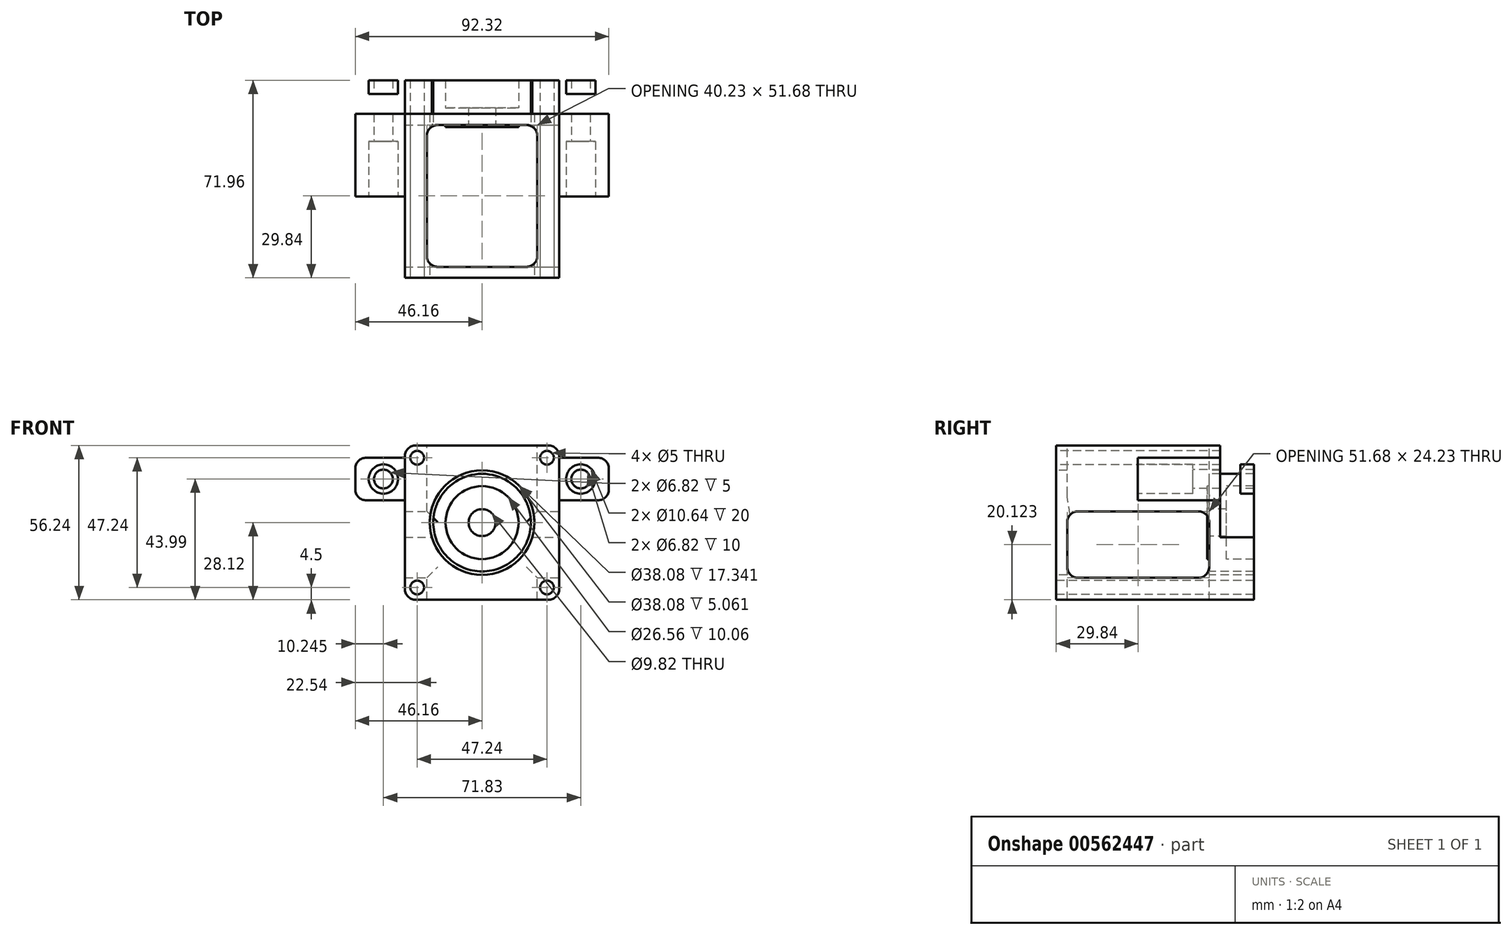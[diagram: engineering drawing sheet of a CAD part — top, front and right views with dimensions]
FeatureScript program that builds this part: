
annotation { "Feature Type Name" : "Feature", "Feature Type Description" : "" }
export const myFeature = defineFeature(function(context is Context, id is Id, definition is map)
    precondition{}
    {
        {
            var Q0;
            Q0=qCreatedBy(makeId("Front.planeOp"),FACE);
            var sketch = newSketch(context, id + "F0", { "sketchPlane" : qUnion([Q0])});
            skLineSegment(sketch, "E0.rect.bottom", {"start": v(-28.11, 28.11) * mm, "end": v(28.12, 28.11) * mm});
            skLineSegment(sketch, "E0.rect.top", {"start": v(-28.12, -28.11) * mm, "end": v(28.11, -28.11) * mm});
            skLineSegment(sketch, "E0.rect.left", {"start": v(-28.11, 28.12) * mm, "end": v(-28.12, -28.11) * mm});
            skLineSegment(sketch, "E0.rect.right", {"start": v(28.12, 28.11) * mm, "end": v(28.11, -28.11) * mm});
            skPoint(sketch, "E0.rect.middle", {"position": v(0, 0) * mm});
            skCircle(sketch, "E1", {"center": v(0, 0) * mm, "radius": 19.04 * mm});
            skCircle(sketch, "E2", {"center": v(0, 0) * mm, "radius": 3.98 * mm});
            skCircle(sketch, "E3", {"center": v(-23.62, 23.62) * mm, "radius": 2.5 * mm});
            skCircle(sketch, "E4", {"center": v(23.62, 23.62) * mm, "radius": 2.5 * mm});
            skCircle(sketch, "E5", {"center": v(23.62, -23.62) * mm, "radius": 2.5 * mm});
            skCircle(sketch, "E6", {"center": v(-23.62, -23.62) * mm, "radius": 2.5 * mm});
            skLineSegment(sketch, "E7.rect.bottom", {"start": v(-23.62, 23.62) * mm, "end": v(23.62, 23.62) * mm, "construction": true});
            skLineSegment(sketch, "E7.rect.top", {"start": v(-23.62, -23.62) * mm, "end": v(23.62, -23.62) * mm, "construction": true});
            skLineSegment(sketch, "E7.rect.left", {"start": v(-23.62, 23.62) * mm, "end": v(-23.62, -23.62) * mm, "construction": true});
            skLineSegment(sketch, "E7.rect.right", {"start": v(23.62, 23.62) * mm, "end": v(23.62, -23.62) * mm, "construction": true});
            skCircle(sketch, "E8", {"center": v(0, 0) * mm, "radius": 5.38 * mm});
            skSolve(sketch);
        }
        {
            var Q0;
            Q0=qCreatedBy(makeId("Front.planeOp"),FACE);
            var sketch = newSketch(context, id + "F1", { "sketchPlane" : qUnion([Q0])});
            skLineSegment(sketch, "E9.bottom", {"start": v(46.15, 37.06) * mm, "end": v(-46.16, 37.06) * mm});
            skLineSegment(sketch, "E9.top", {"start": v(46.16, -5.28) * mm, "end": v(-46.16, -5.28) * mm});
            skLineSegment(sketch, "E9.left", {"start": v(46.15, 37.06) * mm, "end": v(46.16, -5.28) * mm});
            skLineSegment(sketch, "E9.right", {"start": v(-46.16, 37.06) * mm, "end": v(-46.16, -5.28) * mm});
            skCircle(sketch, "E10", {"center": v(0, 0) * mm, "radius": 13.28 * mm});
            skCircle(sketch, "E11", {"center": v(-35.92, 15.87) * mm, "radius": 3.41 * mm});
            skCircle(sketch, "E12", {"center": v(35.91, 15.87) * mm, "radius": 3.41 * mm});
            skCircle(sketch, "E13", {"center": v(-35.92, 15.87) * mm, "radius": 5.32 * mm});
            skCircle(sketch, "E14", {"center": v(35.91, 15.87) * mm, "radius": 5.32 * mm});
            skSolve(sketch);
        }
        {
            var Q0;
            Q0=qCreatedBy(makeId("Front.planeOp"),FACE);
            var sketch = newSketch(context, id + "F2", { "sketchPlane" : qUnion([Q0])});
            skCircle(sketch, "E15", {"center": v(0, 0) * mm, "radius": 4.91 * mm});
            skCircle(sketch, "E16", {"center": v(0, 0) * mm, "radius": 13.28 * mm});
            skCircle(sketch, "E17", {"center": v(0, 0) * mm, "radius": 17.77 * mm});
            skSolve(sketch);
        }
        {
            var Q0;
            Q0=qCreatedBy(makeId("Front.planeOp"),FACE);
            var sketch = newSketch(context, id + "F3", { "sketchPlane" : qUnion([Q0])});
            skLineSegment(sketch, "E18.bottom", {"start": v(-28.11, 28.11) * mm, "end": v(28.12, 28.11) * mm});
            skLineSegment(sketch, "E18.top", {"start": v(-28.11, -5.28) * mm, "end": v(28.12, -5.28) * mm});
            skLineSegment(sketch, "E18.left", {"start": v(-28.11, 28.11) * mm, "end": v(-28.11, -5.28) * mm});
            skLineSegment(sketch, "E18.right", {"start": v(28.12, 28.12) * mm, "end": v(28.12, -5.28) * mm});
            skLineSegment(sketch, "E19.bottom", {"start": v(-28.11, -5.28) * mm, "end": v(28.11, -5.28) * mm});
            skLineSegment(sketch, "E19.top", {"start": v(-28.12, -28.11) * mm, "end": v(28.11, -28.11) * mm});
            skLineSegment(sketch, "E19.left", {"start": v(-28.11, -5.28) * mm, "end": v(-28.11, -28.11) * mm});
            skLineSegment(sketch, "E19.right", {"start": v(28.11, -5.28) * mm, "end": v(28.11, -28.11) * mm});
            skCircle(sketch, "E20", {"center": v(0, 0) * mm, "radius": 19.04 * mm});
            skCircle(sketch, "E21", {"center": v(-23.62, 23.62) * mm, "radius": 2.5 * mm});
            skCircle(sketch, "E22", {"center": v(23.62, 23.62) * mm, "radius": 2.5 * mm});
            skCircle(sketch, "E23", {"center": v(-23.62, -23.62) * mm, "radius": 2.5 * mm});
            skCircle(sketch, "E24", {"center": v(23.62, -23.62) * mm, "radius": 2.5 * mm});
            skLineSegment(sketch, "E25.bottom", {"start": v(46.15, 23.62) * mm, "end": v(28.11, 23.62) * mm});
            skLineSegment(sketch, "E25.top", {"start": v(46.15, 8.12) * mm, "end": v(28.12, 8.12) * mm});
            skLineSegment(sketch, "E25.left", {"start": v(46.15, 23.62) * mm, "end": v(46.15, 8.12) * mm});
            skLineSegment(sketch, "E25.right", {"start": v(28.12, 23.62) * mm, "end": v(28.12, 8.12) * mm});
            skLineSegment(sketch, "E26.bottom", {"start": v(-28.11, 23.62) * mm, "end": v(-46.16, 23.62) * mm});
            skLineSegment(sketch, "E26.top", {"start": v(-28.11, 8.12) * mm, "end": v(-46.16, 8.12) * mm});
            skLineSegment(sketch, "E26.left", {"start": v(-28.11, 23.62) * mm, "end": v(-28.11, 8.12) * mm});
            skLineSegment(sketch, "E26.right", {"start": v(-46.16, 23.62) * mm, "end": v(-46.16, 8.12) * mm});
            skCircle(sketch, "E27", {"center": v(35.91, 15.87) * mm, "radius": 3.41 * mm});
            skCircle(sketch, "E28", {"center": v(35.91, 15.87) * mm, "radius": 5.32 * mm});
            skCircle(sketch, "E29", {"center": v(-35.92, 15.87) * mm, "radius": 5.32 * mm});
            skCircle(sketch, "E30", {"center": v(-35.92, 15.87) * mm, "radius": 3.41 * mm});
            skSolve(sketch);
        }
        {
            var Q0;
            Q0=makeQuery(id+"F3.imprint","IMPRINT",FACE,{"disambiguationData":[TD([[makeQuery(id+"F3.imprint","IMPRINT",EDGE,{"derivedFrom":sQuery(id+"F3.wireOp",EDGE,"E19.top")}),1.0]])]});
            var Q1;
            Q1=makeQuery(id+"FeMlEP8lejCZseU_0.opExtrude","CAP_FACE",FACE,{"disambiguationData":[OSD([sQuery(id+"F1.wireOp",EDGE,"E9.bottom"),sQuery(id+"F1.wireOp",EDGE,"E9.top"),sQuery(id+"F1.wireOp",EDGE,"E9.left"),sQuery(id+"F1.wireOp",EDGE,"E9.right"),sQuery(id+"F1.wireOp",EDGE,"E10"),sQuery(id+"F1.wireOp",EDGE,"E13"),sQuery(id+"F1.wireOp",EDGE,"E14")])],"isStart":false});
            extrude(context, id + "F4", {"entities" : qUnion([Q0]), "oppositeDirection" : true, "endBoundEntityFace" : qUnion([Q1]), "depth" : 42.28 * mm, "hasSecondDirection" : true, "secondDirectionOppositeDirection" : false, "secondDirectionDepth" : 29.68 * mm});
        }
        {
            var Q0;
            Q0=makeQuery(id+"F3.imprint","IMPRINT",FACE,{"disambiguationData":[TD([[makeQuery(id+"F3.imprint","IMPRINT",EDGE,{"derivedFrom":sQuery(id+"F3.wireOp",EDGE,"E18.bottom")}),-1.0]])]});
            var Q1;
            Q1=makeQuery(id+"FeMlEP8lejCZseU_0.opExtrude","CAP_FACE",FACE,{"disambiguationData":[OSD([sQuery(id+"F1.wireOp",EDGE,"E9.bottom"),sQuery(id+"F1.wireOp",EDGE,"E9.top"),sQuery(id+"F1.wireOp",EDGE,"E9.left"),sQuery(id+"F1.wireOp",EDGE,"E9.right"),sQuery(id+"F1.wireOp",EDGE,"E10"),sQuery(id+"F1.wireOp",EDGE,"E13"),sQuery(id+"F1.wireOp",EDGE,"E14")])],"isStart":true});
            extrude(context, id + "F5", {"entities" : qUnion([Q0]), "operationType" : NewBodyOperationType.ADD, "oppositeDirection" : true, "endBoundEntityFace" : qUnion([Q1]), "depth" : 30 * mm, "hasSecondDirection" : true, "secondDirectionOppositeDirection" : false, "secondDirectionDepth" : 29.68 * mm});
        }
        {
            var Q0;
            Q0=makeQuery(id+"F1.imprint","IMPRINT",FACE,{"disambiguationData":[TD([[makeQuery(id+"F1.imprint","IMPRINT",EDGE,{"derivedFrom":sQuery(id+"F1.wireOp",EDGE,"E12")}),-1.0]])]});
            var Q1;
            Q1=makeQuery(id+"F1.imprint","IMPRINT",FACE,{"disambiguationData":[TD([[makeQuery(id+"F1.imprint","IMPRINT",EDGE,{"derivedFrom":sQuery(id+"F1.wireOp",EDGE,"E11")}),-1.0]])]});
            extrude(context, id + "F6", {"entities" : qUnion([Q0, Q1]), "operationType" : NewBodyOperationType.ADD, "oppositeDirection" : true, "depth" : 42.28 * mm, "hasSecondDirection" : true, "secondDirectionOppositeDirection" : true, "secondDirectionDepth" : 37.28 * mm});
        }
        {
            var Q0;
            Q0=makeQuery(id+"F2.imprint","IMPRINT",FACE,{"disambiguationData":[TD([[makeQuery(id+"F2.imprint","IMPRINT",EDGE,{"derivedFrom":sQuery(id+"F2.wireOp",EDGE,"E16")}),-1.0]])]});
            extrude(context, id + "F7", {"entities" : qUnion([Q0]), "operationType" : NewBodyOperationType.ADD, "oppositeDirection" : true, "depth" : 42.28 * mm, "hasSecondDirection" : true, "secondDirectionOppositeDirection" : true, "secondDirectionDepth" : 14.32 * mm});
        }
        {
            var Q0;
            Q0=makeQuery(id+"F3.imprint","IMPRINT",FACE,{"disambiguationData":[TD([[makeQuery(id+"F3.imprint","IMPRINT",EDGE,{"derivedFrom":sQuery(id+"F3.wireOp",EDGE,"E25.bottom")}),1.0]])]});
            var Q1;
            Q1=makeQuery(id+"F3.imprint","IMPRINT",FACE,{"disambiguationData":[TD([[makeQuery(id+"F3.imprint","IMPRINT",EDGE,{"derivedFrom":sQuery(id+"F3.wireOp",EDGE,"E26.bottom")}),1.0]])]});
            extrude(context, id + "F8", {"entities" : qUnion([Q0, Q1]), "operationType" : NewBodyOperationType.ADD, "oppositeDirection" : true, "depth" : 30 * mm});
        }
        {
            var Q0;
            Q0=makeQuery(id+"F1.imprint","IMPRINT",FACE,{"disambiguationData":[TD([[makeQuery(id+"F1.imprint","IMPRINT",EDGE,{"derivedFrom":sQuery(id+"F1.wireOp",EDGE,"E12")}),-1.0]])]});
            var Q1;
            Q1=makeQuery(id+"F1.imprint","IMPRINT",FACE,{"disambiguationData":[TD([[makeQuery(id+"F1.imprint","IMPRINT",EDGE,{"derivedFrom":sQuery(id+"F1.wireOp",EDGE,"E11")}),-1.0]])]});
            extrude(context, id + "F9", {"entities" : qUnion([Q0, Q1]), "operationType" : NewBodyOperationType.ADD, "oppositeDirection" : true, "depth" : 30 * mm, "hasSecondDirection" : true, "secondDirectionOppositeDirection" : true, "secondDirectionDepth" : 20 * mm});
        }
        {
            var Q0;
            Q0=makeQuery(id+"F8.opExtrude","SWEPT_EDGE",EDGE,{"disambiguationData":[OSD([sQuery(id+"F3.wireOp",EDGE,"E26.bottom"),sQuery(id+"F3.wireOp",EDGE,"E26.right")])]});
            var Q1;
            Q1=makeQuery(id+"F8.opExtrude","SWEPT_EDGE",EDGE,{"disambiguationData":[OSD([sQuery(id+"F3.wireOp",EDGE,"E26.top"),sQuery(id+"F3.wireOp",EDGE,"E26.right")])]});
            var Q2;
            Q2=makeQuery(id+"F4.opExtrude","SWEPT_EDGE",EDGE,{"disambiguationData":[OSD([sQuery(id+"F3.wireOp",EDGE,"E19.top"),sQuery(id+"F3.wireOp",EDGE,"E19.left")])]});
            var Q3;
            Q3=makeQuery(id+"F4.opExtrude","SWEPT_EDGE",EDGE,{"disambiguationData":[OSD([sQuery(id+"F3.wireOp",EDGE,"E19.top"),sQuery(id+"F3.wireOp",EDGE,"E19.right")])]});
            var Q4;
            Q4=makeQuery(id+"F8.opExtrude","SWEPT_EDGE",EDGE,{"disambiguationData":[OSD([sQuery(id+"F3.wireOp",EDGE,"E25.top"),sQuery(id+"F3.wireOp",EDGE,"E25.left")])]});
            var Q5;
            Q5=makeQuery(id+"F8.opExtrude","SWEPT_EDGE",EDGE,{"disambiguationData":[OSD([sQuery(id+"F3.wireOp",EDGE,"E25.bottom"),sQuery(id+"F3.wireOp",EDGE,"E25.left")])]});
            var Q6;
            Q6=makeQuery(id+"F5.opExtrude","SWEPT_EDGE",EDGE,{"disambiguationData":[OSD([sQuery(id+"F3.wireOp",EDGE,"E18.bottom"),sQuery(id+"F3.wireOp",EDGE,"E18.right")])]});
            var Q7;
            Q7=makeQuery(id+"F5.opExtrude","SWEPT_EDGE",EDGE,{"disambiguationData":[OSD([sQuery(id+"F3.wireOp",EDGE,"E18.bottom"),sQuery(id+"F3.wireOp",EDGE,"E18.left")])]});
            fillet(context, id + "F10", {"entities" : qUnion([Q0, Q1, Q2, Q3, Q4, Q5, Q6, Q7]), "radius" : 4 * mm, "tangentPropagation" : true, "allowEdgeOverflow" : false});
        }
        {
            var Q0;
            Q0=makeQuery(id+"F5.opExtrude","SWEPT_FACE",FACE,{"disambiguationData":[OSD([sQuery(id+"F3.wireOp",EDGE,"E18.bottom")])]});
            var sketch = newSketch(context, id + "F11", { "sketchPlane" : qUnion([Q0])});
            skLineSegment(sketch, "E31.bottom", {"start": v(-16.11, 26) * mm, "end": v(16.11, 26) * mm});
            skLineSegment(sketch, "E31.top", {"start": v(-16.11, -25.68) * mm, "end": v(16.11, -25.68) * mm});
            skLineSegment(sketch, "E31.left", {"start": v(-20.11, 22) * mm, "end": v(-20.11, -21.68) * mm});
            skLineSegment(sketch, "E31.right", {"start": v(20.11, 22) * mm, "end": v(20.11, -21.68) * mm});
            skPoint(sketch, "E32.visualSharp", {"position": v(-20.11, 26) * mm});
            skArc(sketch, "E32.filletArc", {"start": v(-16.11, 26) * mm, "mid": v(-18.94, 24.83) * mm, "end": v(-20.11, 22) * mm});
            skPoint(sketch, "E33.visualSharp", {"position": v(-20.11, -25.68) * mm});
            skArc(sketch, "E33.filletArc", {"start": v(-20.11, -21.68) * mm, "mid": v(-18.94, -24.5) * mm, "end": v(-16.11, -25.68) * mm});
            skPoint(sketch, "E34.visualSharp", {"position": v(20.11, -25.68) * mm});
            skArc(sketch, "E34.filletArc", {"start": v(16.11, -25.68) * mm, "mid": v(18.94, -24.5) * mm, "end": v(20.11, -21.68) * mm});
            skPoint(sketch, "E35.visualSharp", {"position": v(20.11, 26) * mm});
            skArc(sketch, "E35.filletArc", {"start": v(20.11, 22) * mm, "mid": v(18.94, 24.83) * mm, "end": v(16.11, 26) * mm});
            skSolve(sketch);
        }
        {
            var Q0;
            Q0=qSketchRegion(id+"F11",true);
            var Q1;
            {var subQ0=sQuery(id+"F3.wireOp",EDGE,"E26.left");var subQ1=sQuery(id+"F3.wireOp",EDGE,"E25.right");Q1=makeQuery(id+"F9.boolean.opBoolean","MERGE",FACE,{"derivedFrom":[makeQuery(id+"F8.boolean.opBoolean","MERGE",FACE,{"derivedFrom":[makeQuery(id+"F5.opExtrude","CAP_FACE",FACE,{"disambiguationData":[OSD([sQuery(id+"F3.wireOp",EDGE,"E18.bottom"),sQuery(id+"F3.wireOp",EDGE,"E18.left"),sQuery(id+"F3.wireOp",EDGE,"E18.right"),sQuery(id+"F3.wireOp",EDGE,"E19.bottom"),sQuery(id+"F3.wireOp",EDGE,"E20"),sQuery(id+"F3.wireOp",EDGE,"E21"),sQuery(id+"F3.wireOp",EDGE,"E22"),subQ1,subQ0])],"isStart":false}),makeQuery(id+"F8.opExtrude","CAP_FACE",FACE,{"disambiguationData":[OSD([sQuery(id+"F3.wireOp",EDGE,"E25.bottom"),sQuery(id+"F3.wireOp",EDGE,"E25.top"),sQuery(id+"F3.wireOp",EDGE,"E25.left"),subQ1,sQuery(id+"F3.wireOp",EDGE,"E28")])],"isStart":false}),makeQuery(id+"F8.opExtrude","CAP_FACE",FACE,{"disambiguationData":[OSD([sQuery(id+"F3.wireOp",EDGE,"E26.bottom"),sQuery(id+"F3.wireOp",EDGE,"E26.top"),subQ0,sQuery(id+"F3.wireOp",EDGE,"E26.right"),sQuery(id+"F3.wireOp",EDGE,"E29")])],"isStart":false})]}),makeQuery(id+"F9.opExtrude","CAP_FACE",FACE,{"disambiguationData":[OSD([sQuery(id+"F1.wireOp",EDGE,"E11"),sQuery(id+"F1.wireOp",EDGE,"E13")])],"isStart":false}),makeQuery(id+"F9.opExtrude","CAP_FACE",FACE,{"disambiguationData":[OSD([sQuery(id+"F1.wireOp",EDGE,"E12"),sQuery(id+"F1.wireOp",EDGE,"E14")])],"isStart":false})]});}
            extrude(context, id + "F12", {"entities" : qUnion([Q0]), "operationType" : NewBodyOperationType.REMOVE, "endBound" : BoundingType.THROUGH_ALL, "oppositeDirection" : true, "endBoundEntityFace" : qUnion([Q1]), "depth" : 25 * mm});
        }
        {
            var Q0;
            {var subQ1=sQuery(id+"F3.wireOp",EDGE,"E25.right");var subQ6=sQuery(id+"F3.wireOp",EDGE,"E18.right");var subQ15=sQuery(id+"F3.wireOp",EDGE,"E19.right");var subQ17=sQuery(id+"F3.wireOp",EDGE,"E19.top");Q0=makeQuery(id+"F8.boolean.opBoolean","SPLIT",FACE,{"disambiguationData":[TD([makeQuery(id+"F4.opExtrude","SWEPT_FACE",FACE,{"disambiguationData":[OSD([subQ17])]})])],"derivedFrom":makeQuery(id+"F5.boolean.opBoolean","MERGE",FACE,{"derivedFrom":[makeQuery(id+"F4.opExtrude","SWEPT_FACE",FACE,{"disambiguationData":[OSD([subQ15])]}),makeQuery(id+"F5.opExtrude","SWEPT_FACE",FACE,{"disambiguationData":[OSD([subQ6,subQ1])]})]})});}
            var sketch = newSketch(context, id + "F13", { "sketchPlane" : qUnion([Q0])});
            skLineSegment(sketch, "E36.bottom", {"start": v(-21.68, 4.12) * mm, "end": v(22, 4.12) * mm});
            skLineSegment(sketch, "E36.top", {"start": v(-21.68, -20.11) * mm, "end": v(22, -20.11) * mm});
            skLineSegment(sketch, "E36.left", {"start": v(-25.68, 0.12) * mm, "end": v(-25.68, -16.11) * mm});
            skLineSegment(sketch, "E36.right", {"start": v(26, 0.12) * mm, "end": v(26, -16.11) * mm});
            skPoint(sketch, "E37.visualSharp", {"position": v(-25.68, 4.12) * mm});
            skArc(sketch, "E37.filletArc", {"start": v(-21.68, 4.12) * mm, "mid": v(-24.5, 2.95) * mm, "end": v(-25.68, 0.12) * mm});
            skPoint(sketch, "E38.visualSharp", {"position": v(26, 4.12) * mm});
            skArc(sketch, "E38.filletArc", {"start": v(26, 0.12) * mm, "mid": v(24.83, 2.95) * mm, "end": v(22, 4.12) * mm});
            skPoint(sketch, "E39.visualSharp", {"position": v(26, -20.11) * mm});
            skArc(sketch, "E39.filletArc", {"start": v(22, -20.11) * mm, "mid": v(24.83, -18.94) * mm, "end": v(26, -16.11) * mm});
            skPoint(sketch, "E40.visualSharp", {"position": v(-25.68, -20.11) * mm});
            skArc(sketch, "E40.filletArc", {"start": v(-25.68, -16.11) * mm, "mid": v(-24.5, -18.94) * mm, "end": v(-21.68, -20.11) * mm});
            skSolve(sketch);
        }
        {
            var Q0;
            Q0=qSketchRegion(id+"F13",true);
            extrude(context, id + "F14", {"entities" : qUnion([Q0]), "operationType" : NewBodyOperationType.REMOVE, "endBound" : BoundingType.THROUGH_ALL, "oppositeDirection" : true, "depth" : 25 * mm});
        }
        {
            var Q0;
            Q0=makeQuery(id+"F2.imprint","IMPRINT",FACE,{"disambiguationData":[TD([[makeQuery(id+"F2.imprint","IMPRINT",EDGE,{"derivedFrom":sQuery(id+"F2.wireOp",EDGE,"E15")}),-1.0]])]});
            extrude(context, id + "F15", {"entities" : qUnion([Q0]), "operationType" : NewBodyOperationType.ADD, "oppositeDirection" : true, "depth" : 32.22 * mm, "hasSecondDirection" : true, "secondDirectionOppositeDirection" : true, "secondDirectionDepth" : 25.23 * mm});
        }
    });
